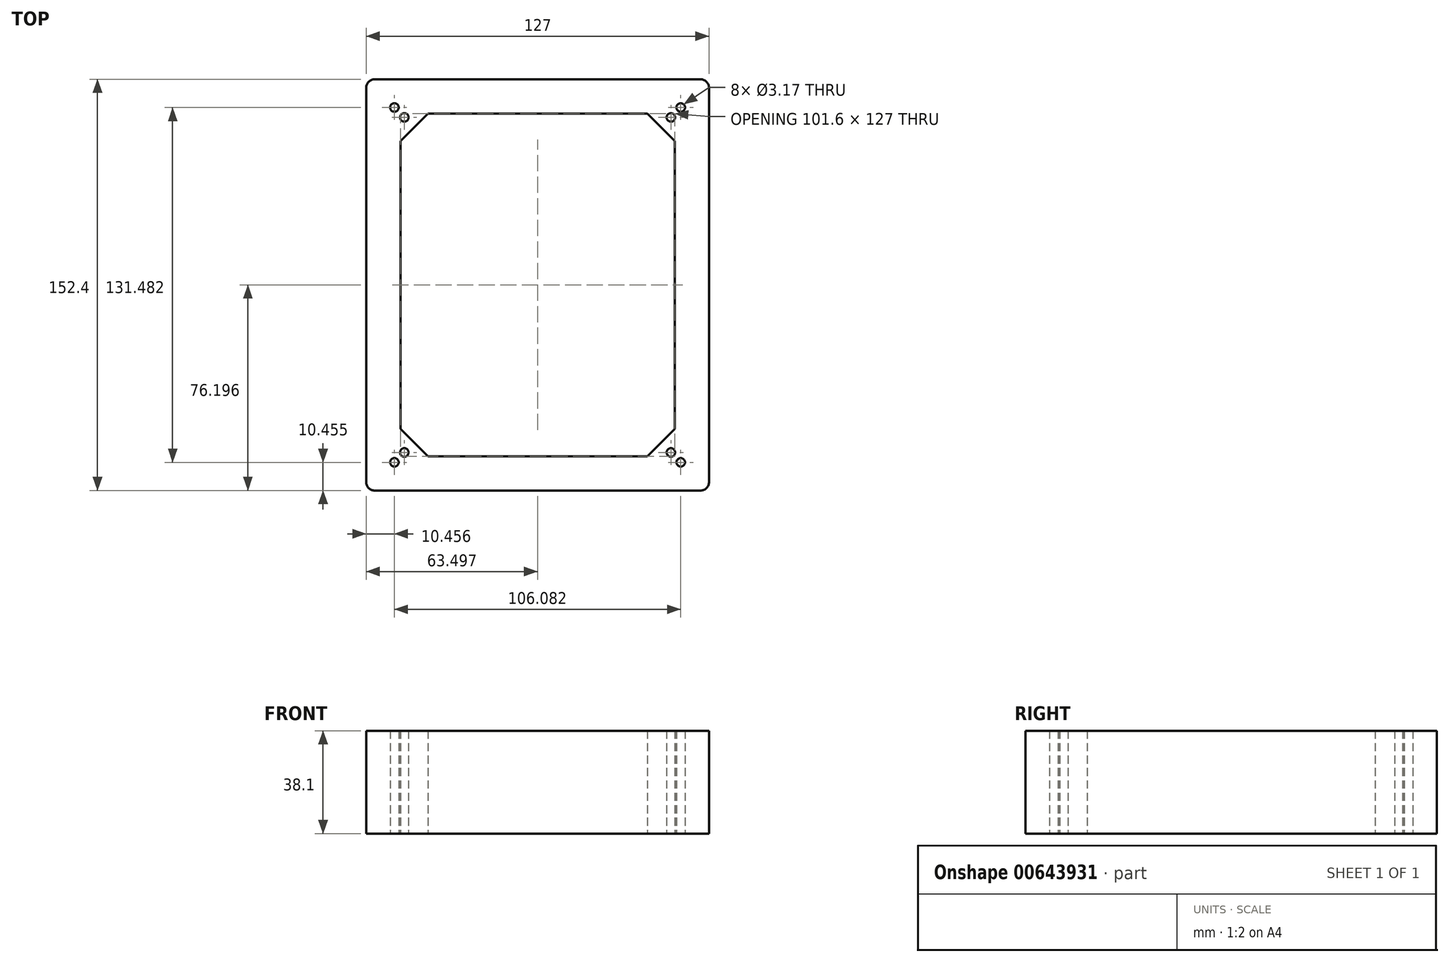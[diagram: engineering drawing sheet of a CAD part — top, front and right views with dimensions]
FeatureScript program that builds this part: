
annotation { "Feature Type Name" : "Feature", "Feature Type Description" : "" }
export const myFeature = defineFeature(function(context is Context, id is Id, definition is map)
    precondition{}
    {
        {
            var Q0;
            Q0=qCreatedBy(makeId("Top.planeOp"),FACE);
            var sketch = newSketch(context, id + "F0", { "sketchPlane" : qUnion([Q0])});
            skLineSegment(sketch, "E0.bottom", {"start": v(-60.12, 76.46) * mm, "end": v(60.53, 76.46) * mm});
            skLineSegment(sketch, "E0.top", {"start": v(-60.12, -75.94) * mm, "end": v(60.53, -75.94) * mm});
            skLineSegment(sketch, "E0.left", {"start": v(-63.3, 73.28) * mm, "end": v(-63.3, -72.77) * mm});
            skLineSegment(sketch, "E0.right", {"start": v(63.7, 73.28) * mm, "end": v(63.7, -72.77) * mm});
            skPoint(sketch, "E0.middle", {"position": v(0.2, 0.26) * mm});
            skLineSegment(sketch, "E1.bottom", {"start": v(-53.77, 70.1) * mm, "end": v(54.18, 70.1) * mm});
            skLineSegment(sketch, "E1.top", {"start": v(-53.77, -69.6) * mm, "end": v(54.18, -69.6) * mm});
            skLineSegment(sketch, "E1.left", {"start": v(-56.94, 66.93) * mm, "end": v(-56.94, -66.42) * mm});
            skLineSegment(sketch, "E1.right", {"start": v(57.36, 66.93) * mm, "end": v(57.36, -66.42) * mm});
            skLineSegment(sketch, "E2.bottom", {"start": v(-47.42, 63.76) * mm, "end": v(47.83, 63.76) * mm});
            skLineSegment(sketch, "E2.top", {"start": v(-47.42, -63.24) * mm, "end": v(48.46, -63.24) * mm});
            skLineSegment(sketch, "E2.left", {"start": v(-50.6, 60.58) * mm, "end": v(-50.6, -60.07) * mm});
            skLineSegment(sketch, "E2.right", {"start": v(51, 60.58) * mm, "end": v(51, -60.7) * mm});
            skPoint(sketch, "E3.visualSharp", {"position": v(-56.94, 70.1) * mm});
            skArc(sketch, "E3.filletArc", {"start": v(-53.77, 70.1) * mm, "mid": v(-56.01, 69.18) * mm, "end": v(-56.94, 66.93) * mm});
            skPoint(sketch, "E4.visualSharp", {"position": v(57.36, 70.1) * mm});
            skArc(sketch, "E4.filletArc", {"start": v(57.36, 66.93) * mm, "mid": v(56.43, 69.18) * mm, "end": v(54.18, 70.1) * mm});
            skPoint(sketch, "E5.visualSharp", {"position": v(57.36, -69.6) * mm});
            skArc(sketch, "E5.filletArc", {"start": v(54.18, -69.6) * mm, "mid": v(56.43, -68.66) * mm, "end": v(57.36, -66.42) * mm});
            skPoint(sketch, "E6.visualSharp", {"position": v(-56.94, -69.6) * mm});
            skArc(sketch, "E6.filletArc", {"start": v(-56.94, -66.42) * mm, "mid": v(-56.01, -68.66) * mm, "end": v(-53.77, -69.6) * mm});
            skPoint(sketch, "E7.visualSharp", {"position": v(51, 63.76) * mm});
            skArc(sketch, "E7.filletArc", {"start": v(51, 60.58) * mm, "mid": v(50.08, 62.83) * mm, "end": v(47.83, 63.76) * mm});
            skPoint(sketch, "E8.visualSharp", {"position": v(51, -63.24) * mm});
            skArc(sketch, "E8.filletArc", {"start": v(48.46, -63.24) * mm, "mid": v(50.26, -62.5) * mm, "end": v(51, -60.7) * mm});
            skPoint(sketch, "E9.visualSharp", {"position": v(-50.6, -63.24) * mm});
            skArc(sketch, "E9.filletArc", {"start": v(-50.6, -60.07) * mm, "mid": v(-49.66, -62.31) * mm, "end": v(-47.42, -63.24) * mm});
            skArc(sketch, "E10.filletArc", {"start": v(-47.42, 63.76) * mm, "mid": v(-49.66, 62.83) * mm, "end": v(-50.6, 60.58) * mm});
            skPoint(sketch, "E11.visualSharp", {"position": v(-63.3, 76.46) * mm});
            skArc(sketch, "E11.filletArc", {"start": v(-60.12, 76.46) * mm, "mid": v(-62.36, 75.53) * mm, "end": v(-63.3, 73.28) * mm});
            skPoint(sketch, "E12.visualSharp", {"position": v(63.7, 76.46) * mm});
            skArc(sketch, "E12.filletArc", {"start": v(63.7, 73.28) * mm, "mid": v(62.78, 75.53) * mm, "end": v(60.53, 76.46) * mm});
            skPoint(sketch, "E13.visualSharp", {"position": v(63.7, -75.94) * mm});
            skArc(sketch, "E13.filletArc", {"start": v(60.53, -75.94) * mm, "mid": v(62.78, -75.01) * mm, "end": v(63.7, -72.77) * mm});
            skPoint(sketch, "E14.visualSharp", {"position": v(-63.3, -75.94) * mm});
            skArc(sketch, "E14.filletArc", {"start": v(-63.3, -72.77) * mm, "mid": v(-62.36, -75.01) * mm, "end": v(-60.12, -75.94) * mm});
            skPoint(sketch, "E15", {"position": v(16.08, 63.76) * mm});
            skPoint(sketch, "E16", {"position": v(16.08, 76.46) * mm});
            skPoint(sketch, "E17", {"position": v(16.08, -63.24) * mm});
            skPoint(sketch, "E18", {"position": v(16.08, -75.94) * mm});
            skPoint(sketch, "E19", {"position": v(-15.67, 76.46) * mm});
            skPoint(sketch, "E20", {"position": v(-15.67, 63.76) * mm});
            skPoint(sketch, "E21", {"position": v(-15.67, -63.24) * mm});
            skPoint(sketch, "E22", {"position": v(-15.67, -75.94) * mm});
            skPoint(sketch, "E23", {"position": v(0.2, 76.46) * mm});
            skPoint(sketch, "E24", {"position": v(0.2, -75.94) * mm});
            skPoint(sketch, "E25", {"position": v(-63.3, 0.26) * mm});
            skPoint(sketch, "E26", {"position": v(63.7, 0.26) * mm});
            skPoint(sketch, "E27", {"position": v(63.7, 16.13) * mm});
            skPoint(sketch, "E28", {"position": v(51, 16.13) * mm});
            skPoint(sketch, "E29", {"position": v(-50.6, 16.13) * mm});
            skPoint(sketch, "E30", {"position": v(-63.3, 16.13) * mm});
            skPoint(sketch, "E31", {"position": v(63.7, -15.62) * mm});
            skPoint(sketch, "E32", {"position": v(51, -15.62) * mm});
            skPoint(sketch, "E33", {"position": v(-50.6, -15.62) * mm});
            skPoint(sketch, "E34", {"position": v(-63.3, -15.62) * mm});
            skPoint(sketch, "E35", {"position": v(40.85, 63.76) * mm});
            skPoint(sketch, "E36", {"position": v(40.85, -63.24) * mm});
            skPoint(sketch, "E37", {"position": v(-40.43, 63.76) * mm});
            skPoint(sketch, "E38", {"position": v(-40.43, -63.24) * mm});
            skPoint(sketch, "E39", {"position": v(-50.6, -53.08) * mm});
            skPoint(sketch, "E40", {"position": v(51, -53.08) * mm});
            skPoint(sketch, "E41", {"position": v(51, 53.6) * mm});
            skPoint(sketch, "E42", {"position": v(-50.6, 53.6) * mm});
            skLineSegment(sketch, "E43", {"start": v(-50.6, 53.6) * mm, "end": v(-40.43, 63.76) * mm});
            skLineSegment(sketch, "E44", {"start": v(40.85, 63.76) * mm, "end": v(51, 53.6) * mm});
            skLineSegment(sketch, "E45", {"start": v(51, -53.08) * mm, "end": v(40.85, -63.24) * mm});
            skLineSegment(sketch, "E46", {"start": v(-40.43, -63.24) * mm, "end": v(-50.6, -53.08) * mm});
            skPoint(sketch, "E47", {"position": v(-45.51, 58.68) * mm});
            skPoint(sketch, "E48", {"position": v(45.93, 58.68) * mm});
            skPoint(sketch, "E49", {"position": v(45.93, -58.16) * mm});
            skPoint(sketch, "E50", {"position": v(-45.51, -58.16) * mm});
            skPoint(sketch, "E51", {"position": v(30.37, 76.46) * mm});
            skPoint(sketch, "E52", {"position": v(30.37, 63.76) * mm});
            skPoint(sketch, "E53", {"position": v(30.37, -63.24) * mm});
            skPoint(sketch, "E54", {"position": v(30.37, -75.94) * mm});
            skPoint(sketch, "E55", {"position": v(-29.96, 76.46) * mm});
            skPoint(sketch, "E56", {"position": v(-29.96, 63.76) * mm});
            skPoint(sketch, "E57", {"position": v(-29.96, -63.24) * mm});
            skPoint(sketch, "E58", {"position": v(-29.96, -75.94) * mm});
            skPoint(sketch, "E59", {"position": v(63.7, 36.77) * mm});
            skPoint(sketch, "E60", {"position": v(51, 36.77) * mm});
            skPoint(sketch, "E61", {"position": v(-50.6, 36.77) * mm});
            skPoint(sketch, "E62", {"position": v(-63.3, 36.77) * mm});
            skPoint(sketch, "E63", {"position": v(63.7, -36.26) * mm});
            skPoint(sketch, "E64", {"position": v(51, -36.26) * mm});
            skPoint(sketch, "E65", {"position": v(-50.6, -36.26) * mm});
            skPoint(sketch, "E66", {"position": v(-63.3, -36.26) * mm});
            skPoint(sketch, "E67", {"position": v(-36.3, 76.46) * mm});
            skPoint(sketch, "E68", {"position": v(-36.3, 63.76) * mm});
            skPoint(sketch, "E69", {"position": v(-36.3, -63.24) * mm});
            skPoint(sketch, "E70", {"position": v(-36.3, -75.94) * mm});
            skPoint(sketch, "E71", {"position": v(36.72, 76.46) * mm});
            skPoint(sketch, "E72", {"position": v(36.72, 63.76) * mm});
            skPoint(sketch, "E73", {"position": v(36.72, -63.24) * mm});
            skPoint(sketch, "E74", {"position": v(36.72, -75.94) * mm});
            skPoint(sketch, "E75", {"position": v(-23.6, 76.46) * mm});
            skPoint(sketch, "E76", {"position": v(-23.6, 63.76) * mm});
            skPoint(sketch, "E77", {"position": v(24.02, 76.46) * mm});
            skPoint(sketch, "E78", {"position": v(24.02, 63.76) * mm});
            skPoint(sketch, "E79", {"position": v(24.02, -63.24) * mm});
            skPoint(sketch, "E80", {"position": v(24.02, -75.94) * mm});
            skPoint(sketch, "E81", {"position": v(-23.6, -63.24) * mm});
            skPoint(sketch, "E82", {"position": v(-23.6, -75.94) * mm});
            skPoint(sketch, "E83", {"position": v(-63.3, 43.12) * mm});
            skPoint(sketch, "E84", {"position": v(-50.6, 43.12) * mm});
            skPoint(sketch, "E85", {"position": v(51, 43.12) * mm});
            skPoint(sketch, "E86", {"position": v(63.7, 43.12) * mm});
            skPoint(sketch, "E87", {"position": v(-63.3, 30.42) * mm});
            skPoint(sketch, "E88", {"position": v(-50.6, 30.42) * mm});
            skPoint(sketch, "E89", {"position": v(51, 30.42) * mm});
            skPoint(sketch, "E90", {"position": v(63.7, 30.42) * mm});
            skPoint(sketch, "E91", {"position": v(-63.3, -29.9) * mm});
            skPoint(sketch, "E92", {"position": v(-50.6, -29.9) * mm});
            skPoint(sketch, "E93", {"position": v(51, -29.9) * mm});
            skPoint(sketch, "E94", {"position": v(63.7, -29.9) * mm});
            skPoint(sketch, "E95", {"position": v(-63.3, -42.6) * mm});
            skPoint(sketch, "E96", {"position": v(-50.6, -42.6) * mm});
            skPoint(sketch, "E97", {"position": v(51, -42.6) * mm});
            skPoint(sketch, "E98", {"position": v(63.7, -42.6) * mm});
            skLineSegment(sketch, "E99", {"start": v(57.36, 70.1) * mm, "end": v(45.93, 58.68) * mm, "construction": true});
            skLineSegment(sketch, "E100", {"start": v(57.36, -69.6) * mm, "end": v(45.93, -58.16) * mm, "construction": true});
            skLineSegment(sketch, "E101", {"start": v(-56.94, -69.6) * mm, "end": v(-45.51, -58.16) * mm, "construction": true});
            skPoint(sketch, "E102", {"position": v(53.25, 66) * mm});
            skLineSegment(sketch, "E103", {"start": v(-56.94, 70.1) * mm, "end": v(-45.51, 58.68) * mm, "construction": true});
            skPoint(sketch, "E104", {"position": v(-52.83, 66) * mm});
            skPoint(sketch, "E105", {"position": v(53.25, -65.48) * mm});
            skPoint(sketch, "E106", {"position": v(-52.83, -65.48) * mm});
            skCircle(sketch, "E107", {"center": v(-52.83, 66) * mm, "radius": 1.59 * mm});
            skCircle(sketch, "E108", {"center": v(53.25, 66) * mm, "radius": 1.59 * mm});
            skCircle(sketch, "E109", {"center": v(53.25, -65.48) * mm, "radius": 1.59 * mm});
            skCircle(sketch, "E110", {"center": v(-52.83, -65.48) * mm, "radius": 1.59 * mm});
            skPoint(sketch, "E111", {"position": v(-49.17, -61.82) * mm});
            skPoint(sketch, "E112", {"position": v(49.58, -61.82) * mm});
            skCircle(sketch, "E113", {"center": v(-49.17, -61.82) * mm, "radius": 1.59 * mm});
            skCircle(sketch, "E114", {"center": v(49.58, -61.82) * mm, "radius": 1.59 * mm});
            skPoint(sketch, "E115", {"position": v(-49.17, 62.33) * mm});
            skPoint(sketch, "E116", {"position": v(49.58, 62.33) * mm});
            skCircle(sketch, "E117", {"center": v(-49.17, 62.33) * mm, "radius": 1.59 * mm});
            skCircle(sketch, "E118", {"center": v(49.58, 62.33) * mm, "radius": 1.59 * mm});
            skSolve(sketch);
        }
        {
            var Q0;
            Q0=makeQuery(id+"F0.imprint","IMPRINT",FACE,{"disambiguationData":[TD([[makeQuery(id+"F0.imprint","IMPRINT",EDGE,{"derivedFrom":sQuery(id+"F0.wireOp",EDGE,"E0.bottom")}),-1.0]])]});
            var Q1;
            Q1=makeQuery(id+"F0.imprint","IMPRINT",FACE,{"disambiguationData":[TD([[makeQuery(id+"F0.imprint","IMPRINT",EDGE,{"derivedFrom":sQuery(id+"F0.wireOp",EDGE,"E1.bottom")}),-1.0]])]});
            var Q2;
            {var subQ5=sQuery(id+"F0.wireOp",EDGE,"E43");Q2=makeQuery(id+"F0.imprint","IMPRINT",FACE,{"disambiguationData":[TD([[makeQuery(id+"F0.imprint","IMPRINT",EDGE,{"derivedFrom":subQ5}),1.0]])]});}
            var Q3;
            {var subQ8=sQuery(id+"F0.wireOp",EDGE,"E44");Q3=makeQuery(id+"F0.imprint","IMPRINT",FACE,{"disambiguationData":[TD([[makeQuery(id+"F0.imprint","IMPRINT",EDGE,{"derivedFrom":subQ8}),1.0]])]});}
            var Q4;
            {var subQ8=sQuery(id+"F0.wireOp",EDGE,"E45");Q4=makeQuery(id+"F0.imprint","IMPRINT",FACE,{"disambiguationData":[TD([[makeQuery(id+"F0.imprint","IMPRINT",EDGE,{"derivedFrom":subQ8}),1.0]])]});}
            var Q5;
            {var subQ5=sQuery(id+"F0.wireOp",EDGE,"E46");Q5=makeQuery(id+"F0.imprint","IMPRINT",FACE,{"disambiguationData":[TD([[makeQuery(id+"F0.imprint","IMPRINT",EDGE,{"derivedFrom":subQ5}),1.0]])]});}
            extrude(context, id + "F1", {"entities" : qUnion([Q0, Q1, Q2, Q3, Q4, Q5]), "depth" : 38.1 * mm, "offsetDistance" : 25.4 * mm});
        }
    });
